# Revit family: IS_TonicII_Multiproduct_BIM_GB_R4306;R4318
name_source: partatom
category: Plumbing Fixtures
revit_build: Autodesk Revit MEP 2014 (Build: 20140709_2115(x64)
units: mm (PartAtom-declared; Revit-internal decimal feet)

## types (10) — shared parameters
Accessories = www.idealspec.co.uk
AreaUnits = millimeters
Assembly Code = C1030200
AssetType = Fixed
BREEAM = No
Brand = Ideal Standard
Category = Furniture
CodePerformance = EN 14749:2005
ConnectionType = Plumbing
Default Elevation = 800 mm  [stored 2.62467 ft]
DurationUnit = year
ECA = No
ExpectedLife = 30
HandleMatl = ISI_IdealStandard_Handle_Silver_Render
IfcExportAs = IfcFurnitureType
IfcExportType = USERDEFINED
InstallationInstructions = www.idealspec.co.uk/resources.html
LinearUnits = millimeters
Manufacturer = Ideal Standard (UK) Ltd
ManufacturerURL = www.idealspec.co.uk
NBSDescription = Bathroom integrated duct work
NBSReference = 45-35-72/320
NettWeight = 7.5 Kg
NominalDepth = 260 mm
NominalHeight = 360 mm  [stored 1.1811 ft]
NominalLength = 480 mm  [stored 1.5748 ft]
NominalWidth = 450 mm
Shape = Rectangular
Size = 360 x 480 x 450 mm
Space = Internal
SpareParts = www.fastpart-spares.co.uk
TMV3 = No
URL = www.idealspec.co.uk
Uniclass2015Description = Bathroom integrated duct work
Uniclass2015Reference = Pr_40_30_78_04
Uniclass2015Version = Products v1.1
Version = 1
VolumeUnits = Litres
WRAS = No
WarrantyDescription = Manufacturers Warranty
WarrantyDurationParts = 5
WarrantyDurationUnit = year
WaterEfficientProduct = No
zero-valued in all types: CWFU, Cost, HWFU

## per-type parameters (varying)
| type | BIMObjectName | BarCode | Color | Description | Features | Finish | LaminateFinish | Model | ModelNumber | ModelReference | Name | ProductInformation |
| R4306FF - Tonic II 450mm Guest Washbasin Unit - Wood Light Brown | ISI_IdealStandard_Furniture_TonicII_R4306FF | 3391500571884 | Light Brown Wood | Tonic II 450mm guest washbasin unit with 1 door , right hand | 450mm guest washbasin unit with 1 door , right hand | Light Brown Wood | ISI_IdealStandard_Furniture_WoodLightBrownFF_Render | R4306FF | R4306FF | Tonic II 450mm guest washbasin unit with 1 door , right hand | ISI_Furniture_TonicII_R4306FF_IdealStandard | www.idealspec.co.uk/datasheets/R4306FF |
| R4306FE - Tonic II 450mm Guest Washbasin Unit - Wood Light Grey | ISI_IdealStandard_Furniture_TonicII_R4306FE | 3391500571891 | Light Grey Wood | Tonic II 450mm guest washbasin unit with 1 door , right hand | 450mm guest washbasin unit with 1 door , right hand | Light Grey Wood | ISI_IdealStandard_Furniture_WoodLightGreyFE_Render | R4306FE | R4306FE | Tonic II 450mm guest washbasin unit with 1 door , right hand | ISI_Furniture_TonicII_R4306FE_IdealStandard | www.idealspec.co.uk/datasheets/R4306FE |
| R4306FC - Tonic II 450mm Guest Washbasin Unit - Gloss Light Brown | ISI_IdealStandard_Furniture_TonicII_R4306FC | 3391500571877 | Light Brown Gloss | Tonic II 450mm guest washbasin unit with 1 door , right hand | 450mm guest washbasin unit with 1 door , right hand | Light Brown Gloss | ISI_IdealStandard_Furniture_GlossLightBrownFC_Render | R4306FC | R4306FC | Tonic II 450mm guest washbasin unit with 1 door , right hand | ISI_Furniture_TonicII_R4306FC_IdealStandard | www.idealspec.co.uk/datasheets/R4306FC |
| R4306FA - Tonic II 450mm Guest Washbasin Unit - Gloss Light Grey | ISI_IdealStandard_Furniture_TonicII_R4306FA | 3391500571860 | Light Grey Gloss | Tonic II 450mm guest washbasin unit with 1 door , right hand | 450mm guest washbasin unit with 1 door , right hand | Light Grey Gloss | ISI_IdealStandard_Furniture_GlossLightGreyFA_Render | R4306FA | R4306FA | Tonic II 450mm guest washbasin unit with 1 door , right hand | ISI_Furniture_TonicII_R4306FA_IdealStandard | www.idealspec.co.uk/datasheets/R4306FA |
| R4306WG - Tonic II 450mm Guest Washbasin Unit - White Gloss | ISI_IdealStandard_Furniture_TonicII_R4306WG | 3391500571853 | Gloss White | Tonic II 450mm guest washbasin unit with 1 door , right hand | 450mm guest washbasin unit with 1 door , right hand | Gloss White | ISI_IdealStandard_Furniture_WhiteGlossWG_Render | R4306WG | R4306WG | Tonic II 450mm guest washbasin unit with 1 door , right hand | ISI_Furniture_TonicII_R4306WG_IdealStandard | www.idealspec.co.uk/datasheets/R4306WG |
| R4318FF - Tonic II 450mm Guest Washbasin Unit - Wood Light Brown | ISI_IdealStandard_Furniture_TonicII_R4318FF | 3391500571938 | Light Brown Wood | Tonic II 450mm guest washbasin unit with 1 door , left hand | 450mm guest washbasin unit with 1 door , left hand | Light Brown Wood | ISI_IdealStandard_Furniture_WoodLightBrownFF_Render | R4318FF | R4318FF | Tonic II 450mm guest washbasin unit with 1 door , left hand | ISI_Furniture_TonicII_R4318FF_IdealStandard | www.idealspec.co.uk/datasheets/R4318FF |
| R4318FE - Tonic II 450mm Guest Washbasin Unit - Wood Light Grey | ISI_IdealStandard_Furniture_TonicII_R4318FE | 3391500571945 | Light Grey Wood | Tonic II 450mm guest washbasin unit with 1 door , left hand | 450mm guest washbasin unit with 1 door , left hand | Light Grey Wood | ISI_IdealStandard_Furniture_WoodLightGreyFE_Render | R4318FE | R4318FE | Tonic II 450mm guest washbasin unit with 1 door , left hand | ISI_Furniture_TonicII_R4318FE_IdealStandard | www.idealspec.co.uk/datasheets/R4318FE |
| R4318FC - Tonic II 450mm Guest Washbasin Unit - Gloss Light Brown | ISI_IdealStandard_Furniture_TonicII_R4318FC | 3391500571921 | Light Brown Gloss | Tonic II 450mm guest washbasin unit with 1 door , left hand | 450mm guest washbasin unit with 1 door , left hand | Light Brown Gloss | ISI_IdealStandard_Furniture_GlossLightBrownFC_Render | R4318FC | R4318FC | Tonic II 450mm guest washbasin unit with 1 door , left hand | ISI_Furniture_TonicII_R4318FC_IdealStandard | www.idealspec.co.uk/datasheets/R4318FC |
| R4318FA - Tonic II 450mm Guest Washbasin Unit - Gloss Light Grey | ISI_IdealStandard_Furniture_TonicII_R4318FA | 3391500571914 | Light Grey Gloss | Tonic II 450mm guest washbasin unit with 1 door , left hand | 450mm guest washbasin unit with 1 door , left hand | Light Grey Gloss | ISI_IdealStandard_Furniture_GlossLightGreyFA_Render | R4318FA | R4318FA | Tonic II 450mm guest washbasin unit with 1 door , left hand | ISI_Furniture_TonicII_R4318FA_IdealStandard | www.idealspec.co.uk/datasheets/R4318FA |
| R4318WG - Tonic II 450mm Guest Washbasin Unit - White Gloss | ISI_IdealStandard_Furniture_TonicII_R4318WG | 3391500571907 | Gloss White | Tonic II 450mm guest washbasin unit with 1 door , left hand | 450mm guest washbasin unit with 1 door , left hand | Gloss White | ISI_IdealStandard_Furniture_WhiteGlossWG_Render | R4318WG | R4318WG | Tonic II 450mm guest washbasin unit with 1 door , left hand | ISI_Furniture_TonicII_R4318WG_IdealStandard | www.idealspec.co.uk/datasheets/R4318WG |

note: [stored X ft] marks values corroborated as IEEE doubles in the binary element streams (Revit-internal decimal feet)

## geometry (parser evidence)
native form markers: Sweep x3
no freeform markers — native parametric forms only
